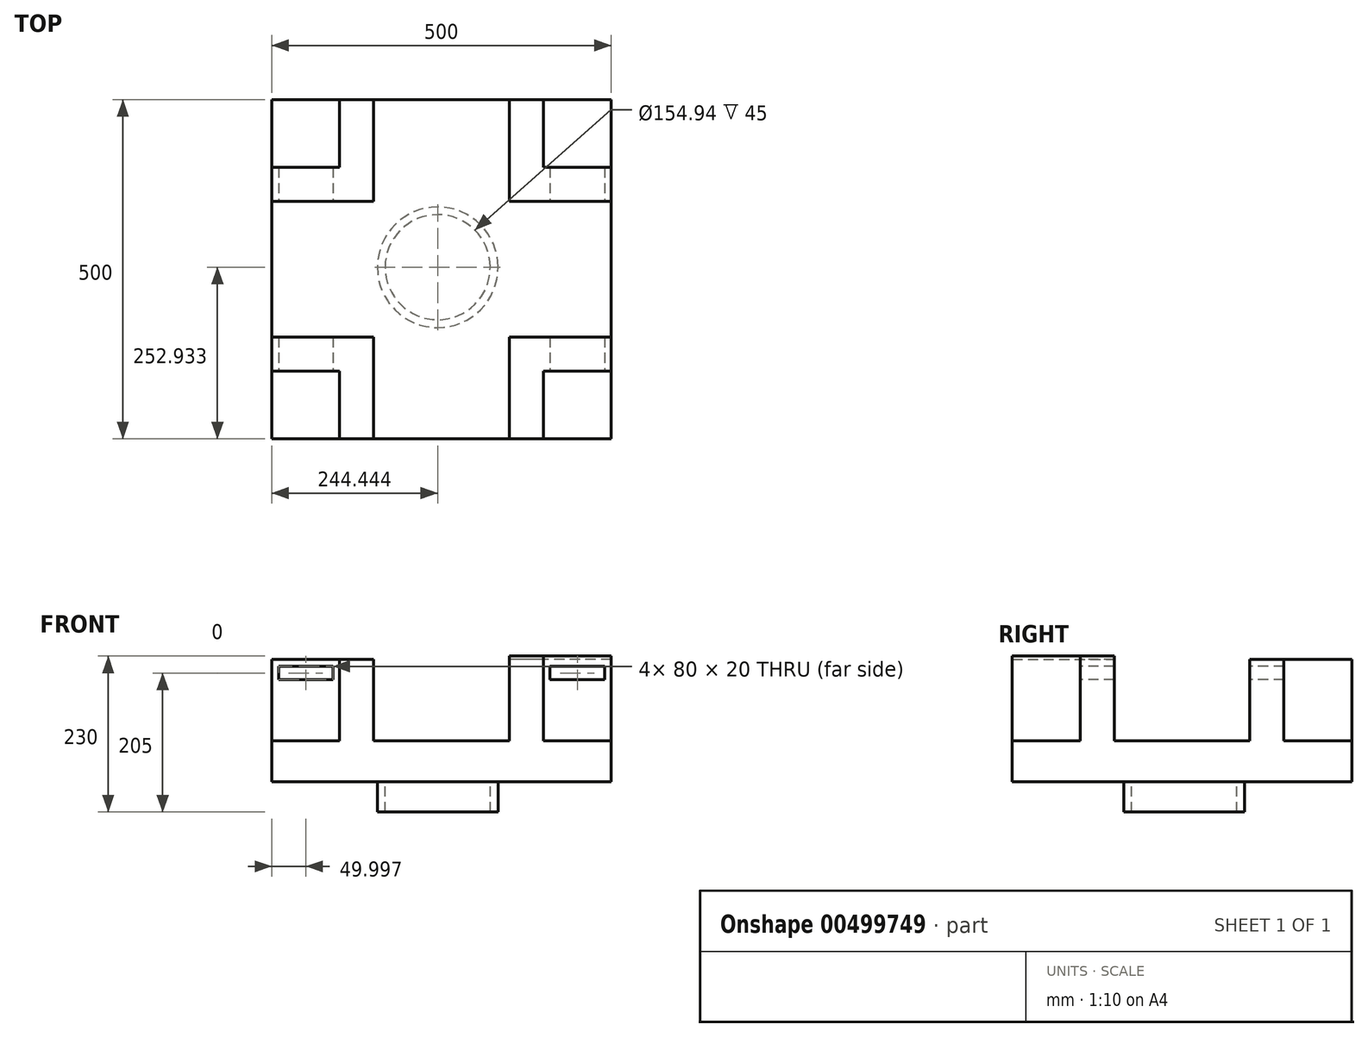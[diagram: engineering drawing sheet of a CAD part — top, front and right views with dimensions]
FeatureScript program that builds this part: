
annotation { "Feature Type Name" : "Feature", "Feature Type Description" : "" }
export const myFeature = defineFeature(function(context is Context, id is Id, definition is map)
    precondition{}
    {
        {
            var Q0;
            Q0=qCreatedBy(makeId("Top.planeOp"),FACE);
            var sketch = newSketch(context, id + "F0", { "sketchPlane" : qUnion([Q0])});
            skLineSegment(sketch, "E0.bottom", {"start": v(219.13, 202.15) * mm, "end": v(-280.87, 202.15) * mm});
            skLineSegment(sketch, "E0.top", {"start": v(219.13, -297.85) * mm, "end": v(-280.87, -297.85) * mm});
            skLineSegment(sketch, "E0.left", {"start": v(219.13, 202.15) * mm, "end": v(219.13, -297.85) * mm});
            skLineSegment(sketch, "E0.right", {"start": v(-280.87, 202.15) * mm, "end": v(-280.87, -297.85) * mm});
            skPoint(sketch, "E0.middle", {"position": v(-30.87, -47.85) * mm});
            skLineSegment(sketch, "E1.top", {"start": v(-280.87, 102.15) * mm, "end": v(-180.87, 102.15) * mm});
            skLineSegment(sketch, "E1.right", {"start": v(-180.87, 202.15) * mm, "end": v(-180.87, 102.15) * mm});
            skLineSegment(sketch, "E2.bottom", {"start": v(-280.87, 202.15) * mm, "end": v(-130.87, 202.15) * mm});
            skLineSegment(sketch, "E2.top", {"start": v(-280.87, 52.15) * mm, "end": v(-130.87, 52.15) * mm});
            skLineSegment(sketch, "E2.left", {"start": v(-280.87, 202.15) * mm, "end": v(-280.87, 52.15) * mm});
            skLineSegment(sketch, "E2.right", {"start": v(-130.87, 202.15) * mm, "end": v(-130.87, 52.15) * mm});
            skLineSegment(sketch, "E3", {"start": v(-280.87, -47.85) * mm, "end": v(219.13, -47.85) * mm, "construction": true});
            skLineSegment(sketch, "E4", {"start": v(-30.87, 202.15) * mm, "end": v(-30.87, -297.85) * mm, "construction": true});
            skLineSegment(sketch, "E5.MirrorCS", {"start": v(219.13, 52.15) * mm, "end": v(69.13, 52.15) * mm});
            skLineSegment(sketch, "E6.MirrorCS", {"start": v(219.13, 102.15) * mm, "end": v(119.13, 102.15) * mm});
            skLineSegment(sketch, "E7.MirrorCS", {"start": v(119.13, 202.15) * mm, "end": v(119.13, 102.15) * mm});
            skLineSegment(sketch, "E8.MirrorCS", {"start": v(69.13, 202.15) * mm, "end": v(69.13, 52.15) * mm});
            skLineSegment(sketch, "E9.MirrorCS", {"start": v(-280.87, -147.85) * mm, "end": v(-130.87, -147.85) * mm});
            skLineSegment(sketch, "E10.MirrorCS", {"start": v(-280.87, -197.85) * mm, "end": v(-180.87, -197.85) * mm});
            skLineSegment(sketch, "E11.MirrorCS", {"start": v(-180.87, -297.85) * mm, "end": v(-180.87, -197.85) * mm});
            skLineSegment(sketch, "E12.MirrorCS", {"start": v(-130.87, -297.85) * mm, "end": v(-130.87, -147.85) * mm});
            skLineSegment(sketch, "E13.MirrorCS", {"start": v(69.13, -297.85) * mm, "end": v(69.13, -147.85) * mm});
            skLineSegment(sketch, "E14.MirrorCS", {"start": v(219.13, -147.85) * mm, "end": v(69.13, -147.85) * mm});
            skLineSegment(sketch, "E15.MirrorCS", {"start": v(219.13, -197.85) * mm, "end": v(119.13, -197.85) * mm});
            skLineSegment(sketch, "E16.MirrorCS", {"start": v(119.13, -297.85) * mm, "end": v(119.13, -197.85) * mm});
            skSolve(sketch);
        }
        {
            var Q0;
            {var subQ0=sQuery(id+"F0.wireOp",EDGE,"E9.MirrorCS");Q0=makeQuery(id+"F0.imprint","IMPRINT",FACE,{"disambiguationData":[TD([[makeQuery(id+"F0.imprint","IMPRINT",EDGE,{"derivedFrom":subQ0}),-1.0]])]});}
            var Q1;
            {var subQ4=sQuery(id+"F0.wireOp",EDGE,"E1.top");Q1=makeQuery(id+"F0.imprint","IMPRINT",FACE,{"disambiguationData":[TD([[makeQuery(id+"F0.imprint","IMPRINT",EDGE,{"derivedFrom":subQ4}),-1.0]])]});}
            var Q2;
            {var subQ1=sQuery(id+"F0.wireOp",EDGE,"E5.MirrorCS");Q2=makeQuery(id+"F0.imprint","IMPRINT",FACE,{"disambiguationData":[TD([[makeQuery(id+"F0.imprint","IMPRINT",EDGE,{"derivedFrom":subQ1}),-1.0]])]});}
            var Q3;
            {var subQ3=sQuery(id+"F0.wireOp",EDGE,"E13.MirrorCS");Q3=makeQuery(id+"F0.imprint","IMPRINT",FACE,{"disambiguationData":[TD([[makeQuery(id+"F0.imprint","IMPRINT",EDGE,{"derivedFrom":subQ3}),-1.0]])]});}
            extrude(context, id + "F1", {"entities" : qUnion([Q0, Q1, Q2, Q3]), "depth" : 125 * mm});
        }
        {
            var Q0;
            {var subQ5=sQuery(id+"F0.wireOp",EDGE,"E2.top");Q0=makeQuery(id+"F0.imprint","IMPRINT",FACE,{"disambiguationData":[TD([[makeQuery(id+"F0.imprint","IMPRINT",EDGE,{"derivedFrom":subQ5}),-1.0]])]});}
            var Q1;
            Q1=makeQuery(id+"F1.opExtrude","CAP_FACE",FACE,{"disambiguationData":[OSD([sQuery(id+"F0.wireOp",EDGE,"E0.top"),sQuery(id+"F0.wireOp",EDGE,"E0.left"),sQuery(id+"F0.wireOp",EDGE,"E13.MirrorCS"),sQuery(id+"F0.wireOp",EDGE,"E14.MirrorCS"),sQuery(id+"F0.wireOp",EDGE,"E15.MirrorCS"),sQuery(id+"F0.wireOp",EDGE,"E16.MirrorCS")])],"isStart":false});
            var Q2;
            {var subQ4=sQuery(id+"F0.wireOp",EDGE,"E1.top");Q2=makeQuery(id+"F0.imprint","IMPRINT",FACE,{"disambiguationData":[TD([[makeQuery(id+"F0.imprint","IMPRINT",EDGE,{"derivedFrom":subQ4}),-1.0]])]});}
            var Q3;
            {var subQ0=sQuery(id+"F0.wireOp",EDGE,"E1.top");Q3=makeQuery(id+"F0.imprint","IMPRINT",FACE,{"disambiguationData":[TD([[makeQuery(id+"F0.imprint","IMPRINT",EDGE,{"derivedFrom":subQ0}),1.0]])]});}
            var Q4;
            {var subQ4=sQuery(id+"F0.wireOp",EDGE,"E10.MirrorCS");Q4=makeQuery(id+"F0.imprint","IMPRINT",FACE,{"disambiguationData":[TD([[makeQuery(id+"F0.imprint","IMPRINT",EDGE,{"derivedFrom":subQ4}),-1.0]])]});}
            var Q5;
            {var subQ0=sQuery(id+"F0.wireOp",EDGE,"E9.MirrorCS");Q5=makeQuery(id+"F0.imprint","IMPRINT",FACE,{"disambiguationData":[TD([[makeQuery(id+"F0.imprint","IMPRINT",EDGE,{"derivedFrom":subQ0}),-1.0]])]});}
            var Q6;
            {var subQ4=sQuery(id+"F0.wireOp",EDGE,"E6.MirrorCS");Q6=makeQuery(id+"F0.imprint","IMPRINT",FACE,{"disambiguationData":[TD([[makeQuery(id+"F0.imprint","IMPRINT",EDGE,{"derivedFrom":subQ4}),-1.0]])]});}
            var Q7;
            {var subQ1=sQuery(id+"F0.wireOp",EDGE,"E5.MirrorCS");Q7=makeQuery(id+"F0.imprint","IMPRINT",FACE,{"disambiguationData":[TD([[makeQuery(id+"F0.imprint","IMPRINT",EDGE,{"derivedFrom":subQ1}),-1.0]])]});}
            var Q8;
            {var subQ4=sQuery(id+"F0.wireOp",EDGE,"E15.MirrorCS");Q8=makeQuery(id+"F0.imprint","IMPRINT",FACE,{"disambiguationData":[TD([[makeQuery(id+"F0.imprint","IMPRINT",EDGE,{"derivedFrom":subQ4}),1.0]])]});}
            var Q9;
            {var subQ3=sQuery(id+"F0.wireOp",EDGE,"E13.MirrorCS");Q9=makeQuery(id+"F0.imprint","IMPRINT",FACE,{"disambiguationData":[TD([[makeQuery(id+"F0.imprint","IMPRINT",EDGE,{"derivedFrom":subQ3}),-1.0]])]});}
            extrude(context, id + "F2", {"entities" : qUnion([Q0, Q1, Q2, Q3, Q4, Q5, Q6, Q7, Q8, Q9]), "operationType" : NewBodyOperationType.ADD, "oppositeDirection" : true, "depth" : 50 * mm, "hasSecondDirection" : true, "secondDirectionOppositeDirection" : false, "secondDirectionDepth" : 5 * mm});
        }
        {
            var Q0;
            Q0=makeQuery(id+"F2.opExtrude","CAP_FACE",FACE,{"disambiguationData":[OSD([sQuery(id+"F0.wireOp",EDGE,"E0.bottom"),sQuery(id+"F0.wireOp",EDGE,"E0.top"),sQuery(id+"F0.wireOp",EDGE,"E0.left"),sQuery(id+"F0.wireOp",EDGE,"E0.right"),sQuery(id+"F0.wireOp",EDGE,"E2.bottom"),sQuery(id+"F0.wireOp",EDGE,"E2.left")])],"isStart":false});
            var sketch = newSketch(context, id + "F3", { "sketchPlane" : qUnion([Q0])});
            skCircle(sketch, "E17", {"center": v(-36.43, 44.92) * mm, "radius": 77.47 * mm});
            skCircle(sketch, "E18", {"center": v(-36.43, 44.92) * mm, "radius": 88.9 * mm});
            skSolve(sketch);
        }
        {
            var Q0;
            Q0 = qSketchRegion(id + "F3", true);
            extrude(context, id + "F4", {"entities" : qUnion([Q0]), "depth" : 50 * mm});
        }
        {
            var Q0;
            Q0=makeQuery(id+"F3.imprint","IMPRINT",FACE,{"disambiguationData":[TD([[makeQuery(id+"F3.imprint","IMPRINT",EDGE,{"derivedFrom":sQuery(id+"F3.wireOp",EDGE,"E17")}),1.0]])]});
            var Q1;
            {var subQ0=sQuery(id+"F0.wireOp",EDGE,"E0.bottom");Q1=makeQuery(id+"F3.imprint","IMPRINT",FACE,{"disambiguationData":[TD([[makeQuery(id+"F3.imprint","IMPRINT",EDGE,{"derivedFrom":makeQuery(id+"F2.opExtrude","CAP_EDGE",EDGE,{"disambiguationData":[OSD([subQ0,sQuery(id+"F0.wireOp",EDGE,"E2.bottom")])],"isStart":false})}),-1.0]])]});}
            extrude(context, id + "F5", {"entities" : qUnion([Q0, Q1]), "operationType" : NewBodyOperationType.ADD, "depth" : 5 * mm, "hasSecondDirection" : true, "secondDirectionOppositeDirection" : true, "secondDirectionDepth" : 5 * mm});
        }
        {
            var Q0;
            Q0=makeQuery(id+"F1.opExtrude","SWEPT_FACE",FACE,{"disambiguationData":[OSD([sQuery(id+"F0.wireOp",EDGE,"E10.MirrorCS")])]});
            var sketch = newSketch(context, id + "F6", { "sketchPlane" : qUnion([Q0])});
            skLineSegment(sketch, "E19.bottom", {"start": v(-270.87, 115) * mm, "end": v(-190.87, 115) * mm});
            skLineSegment(sketch, "E19.top", {"start": v(-270.87, 95) * mm, "end": v(-190.87, 95) * mm});
            skLineSegment(sketch, "E19.left", {"start": v(-270.87, 115) * mm, "end": v(-270.87, 95) * mm});
            skLineSegment(sketch, "E19.right", {"start": v(-190.87, 115) * mm, "end": v(-190.87, 95) * mm});
            skLineSegment(sketch, "E20", {"start": v(-30.87, 0) * mm, "end": v(-30.87, 154.38) * mm, "construction": true});
            skLineSegment(sketch, "E21.MirrorCS", {"start": v(209.13, 115) * mm, "end": v(129.13, 115) * mm});
            skLineSegment(sketch, "E22.MirrorCS", {"start": v(209.13, 95) * mm, "end": v(129.13, 95) * mm});
            skLineSegment(sketch, "E23.MirrorCS", {"start": v(129.13, 115) * mm, "end": v(129.13, 95) * mm});
            skLineSegment(sketch, "E24.MirrorCS", {"start": v(209.13, 115) * mm, "end": v(209.13, 95) * mm});
            skSolve(sketch);
        }
        {
            var Q0;
            Q0 = qSketchRegion(id + "F6", true);
            extrude(context, id + "F7", {"entities" : qUnion([Q0]), "operationType" : NewBodyOperationType.REMOVE, "oppositeDirection" : true, "depth" : 23000 * mm});
        }
    });
